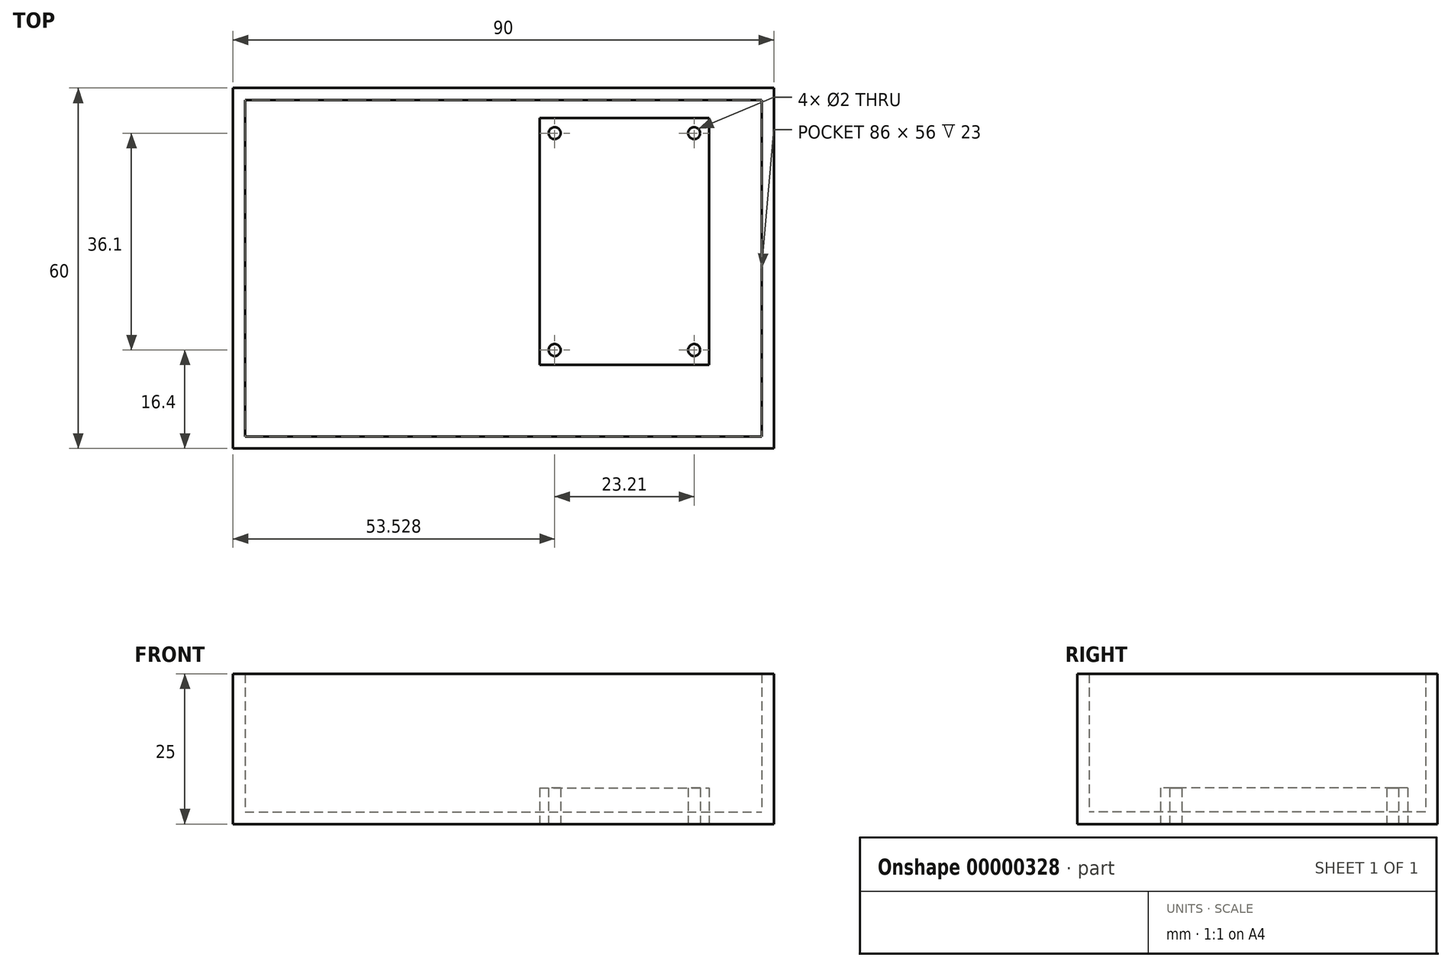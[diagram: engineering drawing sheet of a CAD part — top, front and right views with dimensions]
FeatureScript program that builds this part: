
annotation { "Feature Type Name" : "Feature", "Feature Type Description" : "" }
export const myFeature = defineFeature(function(context is Context, id is Id, definition is map)
    precondition{}
    {
        {
            var Q0;
            Q0=qCreatedBy(makeId("Top.planeOp"),FACE);
            var sketch = newSketch(context, id + "F0", { "sketchPlane" : qUnion([Q0])});
            skLineSegment(sketch, "E0.bottom", {"start": v(-17.31, 0) * mm, "end": v(10.9, 0) * mm});
            skLineSegment(sketch, "E0.top", {"start": v(-17.31, -41.1) * mm, "end": v(10.9, -41.1) * mm});
            skLineSegment(sketch, "E0.left", {"start": v(-17.31, 0) * mm, "end": v(-17.31, -41.1) * mm});
            skLineSegment(sketch, "E0.right", {"start": v(10.9, 0) * mm, "end": v(10.9, -41.1) * mm});
            skCircle(sketch, "E1", {"center": v(-14.81, -2.5) * mm, "radius": 1 * mm});
            skCircle(sketch, "E2", {"center": v(8.4, -2.5) * mm, "radius": 1 * mm});
            skCircle(sketch, "E3", {"center": v(-14.81, -38.6) * mm, "radius": 1 * mm});
            skCircle(sketch, "E4", {"center": v(8.4, -38.6) * mm, "radius": 1 * mm});
            skSolve(sketch);
        }
        {
            var Q0;
            Q0=qCreatedBy(makeId("Top.planeOp"),FACE);
            var sketch = newSketch(context, id + "F1", { "sketchPlane" : qUnion([Q0])});
            skLineSegment(sketch, "E5.bottom", {"start": v(-63.34, 0) * mm, "end": v(-26.27, 0) * mm});
            skLineSegment(sketch, "E5.top", {"start": v(-63.34, -51.8) * mm, "end": v(-26.27, -51.8) * mm});
            skLineSegment(sketch, "E5.left", {"start": v(-63.34, 0) * mm, "end": v(-63.34, -51.8) * mm});
            skLineSegment(sketch, "E5.right", {"start": v(-26.27, 0) * mm, "end": v(-26.27, -51.8) * mm});
            skPoint(sketch, "E6", {"position": v(-26.27, -25.9) * mm});
            skSolve(sketch);
        }
        {
            var Q0;
            Q0=makeQuery(id+"F0.imprint","IMPRINT",FACE,{"disambiguationData":[TD([[makeQuery(id+"F0.imprint","IMPRINT",EDGE,{"derivedFrom":sQuery(id+"F0.wireOp",EDGE,"E0.bottom")}),-1.0]])]});
            extrude(context, id + "F2", {"entities" : qUnion([Q0]), "depth" : 6 * mm});
        }
        {
            var Q0;
            Q0=makeQuery(id+"F1.imprint","IMPRINT",FACE,{"disambiguationData":[TD([[makeQuery(id+"F1.imprint","IMPRINT",EDGE,{"derivedFrom":sQuery(id+"F1.wireOp",EDGE,"E5.bottom")}),-1.0]])]});
            extrude(context, id + "F3", {"entities" : qUnion([Q0]), "depth" : 13.5 * mm});
        }
        {
            var Q0;
            Q0=qCreatedBy(makeId("Top.planeOp"),FACE);
            var sketch = newSketch(context, id + "F4", { "sketchPlane" : qUnion([Q0])});
            skLineSegment(sketch, "E7.bottom", {"start": v(-68.34, 5) * mm, "end": v(21.66, 5) * mm});
            skLineSegment(sketch, "E7.top", {"start": v(-68.34, -55) * mm, "end": v(21.66, -55) * mm});
            skLineSegment(sketch, "E7.left", {"start": v(-68.34, 5) * mm, "end": v(-68.34, -55) * mm});
            skLineSegment(sketch, "E7.right", {"start": v(21.66, 5) * mm, "end": v(21.66, -55) * mm});
            skSolve(sketch);
        }
        {
            var Q0;
            Q0=makeQuery(id+"F4.imprint","IMPRINT",FACE,{"disambiguationData":[TD([[makeQuery(id+"F4.imprint","IMPRINT",EDGE,{"derivedFrom":sQuery(id+"F4.wireOp",EDGE,"E7.bottom")}),-1.0]])]});
            extrude(context, id + "F5", {"entities" : qUnion([Q0]), "depth" : 25 * mm});
        }
        {
            var Q0;
            Q0=makeQuery(id+"F5.opExtrude","CAP_FACE",FACE,{"disambiguationData":[OSD([sQuery(id+"F4.wireOp",EDGE,"E7.bottom"),sQuery(id+"F4.wireOp",EDGE,"E7.top"),sQuery(id+"F4.wireOp",EDGE,"E7.left"),sQuery(id+"F4.wireOp",EDGE,"E7.right")])],"isStart":false});
            shell(context, id + "F6", {"entities" : qUnion([Q0]), "thickness" : 2 * mm});
        }
        {
            var Q0;
            Q0=makeQuery(id+"F3.opExtrude","SWEPT_BODY",BODY,{"disambiguationData":[OSD([sQuery(id+"F1.wireOp",EDGE,"E5.bottom"),sQuery(id+"F1.wireOp",EDGE,"E5.top"),sQuery(id+"F1.wireOp",EDGE,"E5.left"),sQuery(id+"F1.wireOp",EDGE,"E5.right")])]});
            deleteBodies(context, id + "F7", {"entities" : qUnion([Q0])});
        }
    });
